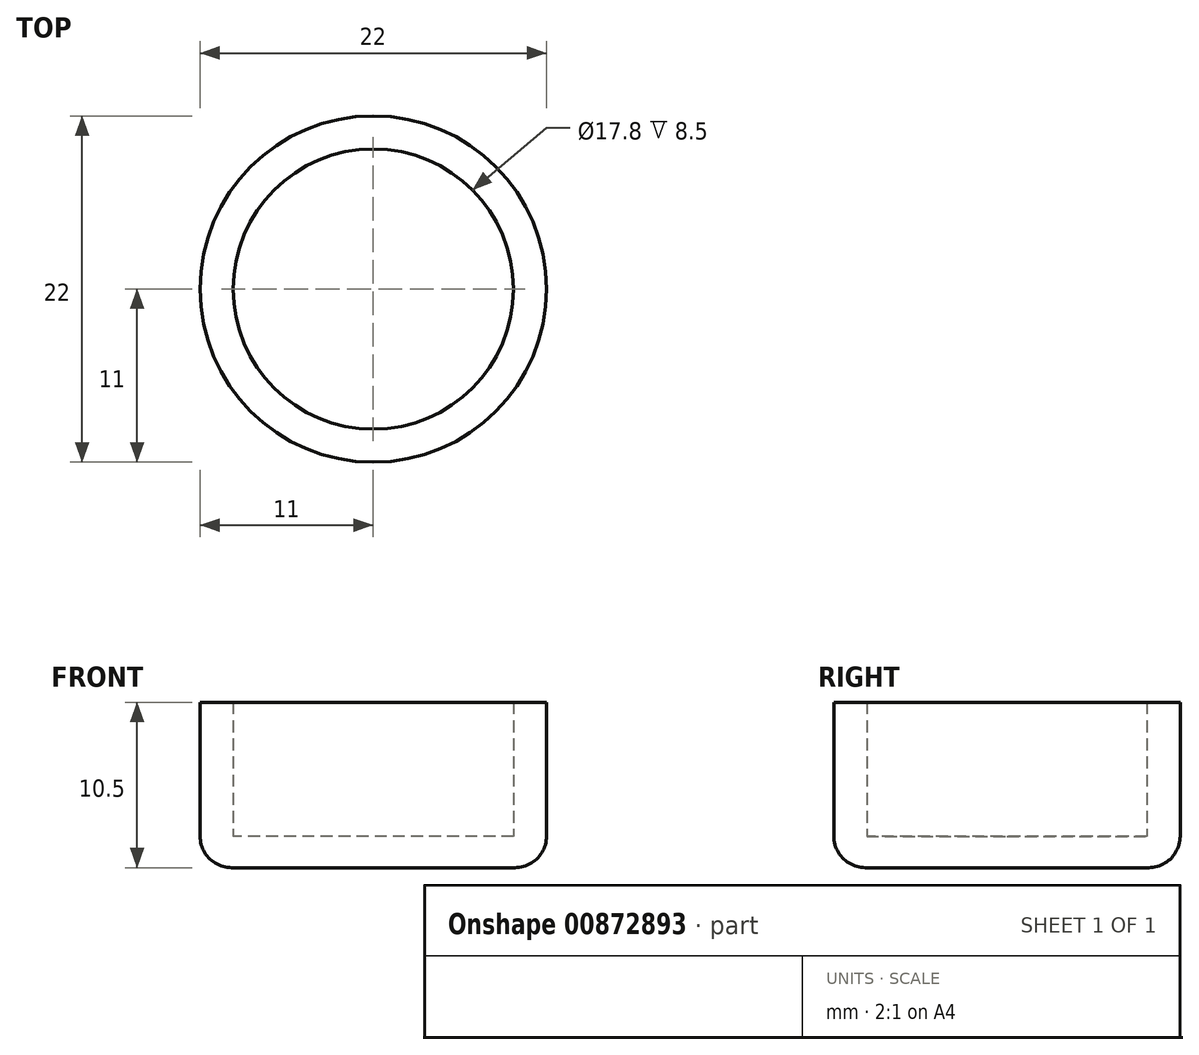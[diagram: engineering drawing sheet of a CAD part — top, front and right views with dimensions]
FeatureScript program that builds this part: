
annotation { "Feature Type Name" : "Feature", "Feature Type Description" : "" }
export const myFeature = defineFeature(function(context is Context, id is Id, definition is map)
    precondition{}
    {
        {
            var Q0;
            Q0=qCreatedBy(makeId("Top.planeOp"),FACE);
            var sketch = newSketch(context, id + "F0", { "sketchPlane" : qUnion([Q0])});
            skCircle(sketch, "E0", {"center": v(0, 0) * mm, "radius": 8.9 * mm});
            skCircle(sketch, "E1", {"center": v(0, 0) * mm, "radius": 11 * mm});
            skSolve(sketch);
        }
        {
            var Q0;
            Q0=makeQuery(id+"F0.imprint","IMPRINT",FACE,{"disambiguationData":[TD([[makeQuery(id+"F0.imprint","IMPRINT",EDGE,{"derivedFrom":sQuery(id+"F0.wireOp",EDGE,"E0")}),1.0]])]});
            var Q1;
            Q1=sQuery(id+"F0.wireOp",EDGE,"E0");
            extrude(context, id + "F1", {"entities" : qUnion([Q0]), "surfaceEntities" : qUnion([Q1]), "depth" : 2 * mm, "offsetDistance" : 25 * mm});
        }
        {
            var Q0;
            Q0=makeQuery(id+"F0.imprint","IMPRINT",FACE,{"disambiguationData":[TD([[makeQuery(id+"F0.imprint","IMPRINT",EDGE,{"derivedFrom":sQuery(id+"F0.wireOp",EDGE,"E0")}),-1.0]])]});
            extrude(context, id + "F2", {"entities" : qUnion([Q0]), "operationType" : NewBodyOperationType.ADD, "depth" : 10.5 * mm, "offsetDistance" : 25 * mm});
        }
        {
            var Q0;
            Q0=makeQuery(id+"F2.opExtrude","CAP_EDGE",EDGE,{"disambiguationData":[OSD([sQuery(id+"F0.wireOp",EDGE,"E1")])],"isStart":true});
            fillet(context, id + "F3", {"entities" : qUnion([Q0]), "radius" : 2 * mm, "tangentPropagation" : true, "allowEdgeOverflow" : false});
        }
    });
